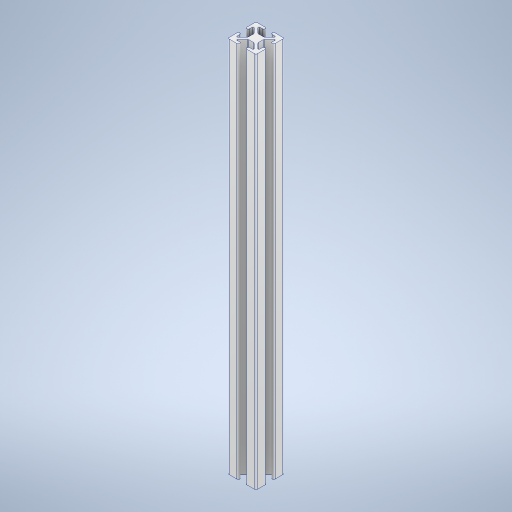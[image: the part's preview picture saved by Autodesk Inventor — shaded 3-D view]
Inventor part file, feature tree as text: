
AUTODESK INVENTOR PART (.ipt)
format: ipt  version: 2024 (Build 280153000, 153)  size: 345,088 bytes
history: native  units: in
note: dims shown in document units (in); Inventor stores cm internally (conversion verified against a paired STEP export)
features: fillet x2, extrude x1, sketch x1
ambient origin geometry x8: Origin, YZ Plane, XZ Plane, XY Plane, X Axis, Y Axis, Z Axis, Center Point
bodies: Solid1 (feature_tree)
feature tree (4):
  extrude  "Extrusion1"  Depth=1.0in
  fillet  "Fillet1"  Radius=0.8in
  fillet  "Fillet2"  Radius=0.8in
  sketch  "Sketch1"  dims[d0=1.0in d1=1.0in d2=0.8in d3=0.8in d4=0.35in d5=0.35in d6=0.125in d7=0.25in d8=0.125in d9=0.25in d10=0.1in d11=0.1in d12=13.35in d13=0.0in d14=0.05in d15=0.025in]
